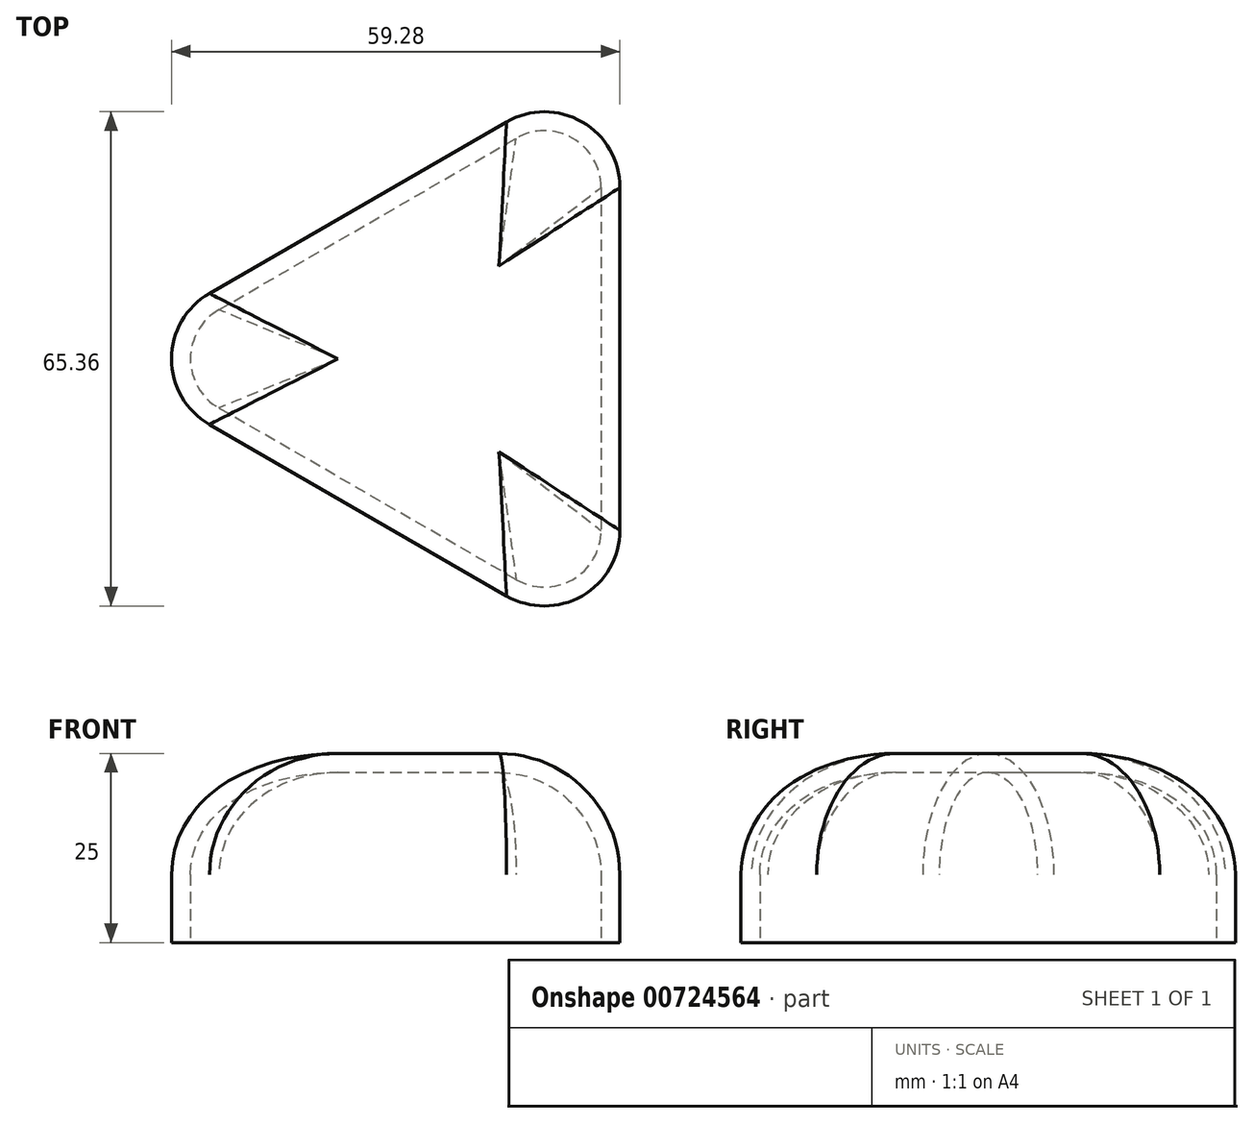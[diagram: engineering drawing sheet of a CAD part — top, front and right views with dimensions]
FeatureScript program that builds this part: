
annotation { "Feature Type Name" : "Feature", "Feature Type Description" : "" }
export const myFeature = defineFeature(function(context is Context, id is Id, definition is map)
    precondition{}
    {
        {
            var Q0;
            Q0=qCreatedBy(makeId("Top.planeOp"),FACE);
            var sketch = newSketch(context, id + "F0", { "sketchPlane" : qUnion([Q0])});
            skCircle(sketch, "E0.cCircle", {"center": v(0, 0) * mm, "radius": 23.1 * mm, "construction": true});
            skLineSegment(sketch, "E0.0", {"start": v(23.1, 40) * mm, "end": v(23.1, -40) * mm});
            skLineSegment(sketch, "E0.1", {"start": v(23.1, -40) * mm, "end": v(-46.19, 0) * mm});
            skLineSegment(sketch, "E0.2", {"start": v(-46.19, 0) * mm, "end": v(23.1, 40) * mm});
            skPoint(sketch, "E0.0.midPoint", {"position": v(23.1, 0) * mm});
            skSolve(sketch);
        }
        {
            var Q0;
            Q0=makeQuery(id+"F0.imprint","IMPRINT",FACE,{"disambiguationData":[TD([[makeQuery(id+"F0.imprint","IMPRINT",EDGE,{"derivedFrom":sQuery(id+"F0.wireOp",EDGE,"E0.0")}),-1.0]])]});
            extrude(context, id + "F1", {"entities" : qUnion([Q0]), "depth" : 25 * mm, "offsetDistance" : 25 * mm});
        }
        {
            var Q0;
            Q0=makeQuery(id+"F1.opExtrude","SWEPT_EDGE",EDGE,{"disambiguationData":[OSD([sQuery(id+"F0.wireOp",EDGE,"E0.0"),sQuery(id+"F0.wireOp",EDGE,"E0.1")])]});
            var Q1;
            Q1=makeQuery(id+"F1.opExtrude","SWEPT_EDGE",EDGE,{"disambiguationData":[OSD([sQuery(id+"F0.wireOp",EDGE,"E0.0"),sQuery(id+"F0.wireOp",EDGE,"E0.2")])]});
            var Q2;
            Q2=makeQuery(id+"F1.opExtrude","SWEPT_EDGE",EDGE,{"disambiguationData":[OSD([sQuery(id+"F0.wireOp",EDGE,"E0.1"),sQuery(id+"F0.wireOp",EDGE,"E0.2")])]});
            fillet(context, id + "F2", {"entities" : qUnion([Q0, Q1, Q2]), "radius" : 10 * mm, "tangentPropagation" : true, "allowEdgeOverflow" : false});
        }
        {
            var Q0;
            {var subQ0=sQuery(id+"F0.wireOp",EDGE,"E0.1");var subQ1=sQuery(id+"F0.wireOp",EDGE,"E0.0");Q0=makeQuery(id+"F2.opFillet","BLEND_EDGE",EDGE,{"blendedFrom":[makeQuery(id+"F1.opExtrude","SWEPT_EDGE",EDGE,{"disambiguationData":[OSD([subQ1,subQ0])]}),makeQuery(id+"F1.opExtrude","CAP_FACE",FACE,{"disambiguationData":[OSD([subQ1,subQ0,sQuery(id+"F0.wireOp",EDGE,"E0.2")])],"isStart":false})],"blendedInto":[makeQuery(id+"F1.opExtrude","CAP_FACE",FACE,{"disambiguationData":[OSD([subQ1,subQ0,sQuery(id+"F0.wireOp",EDGE,"E0.2")])],"isStart":false})]});}
            var Q1;
            Q1=makeQuery(id+"F1.opExtrude","CAP_EDGE",EDGE,{"disambiguationData":[OSD([sQuery(id+"F0.wireOp",EDGE,"E0.0")])],"isStart":false});
            var Q2;
            {var subQ0=sQuery(id+"F0.wireOp",EDGE,"E0.2");var subQ1=sQuery(id+"F0.wireOp",EDGE,"E0.0");Q2=makeQuery(id+"F2.opFillet","BLEND_EDGE",EDGE,{"blendedFrom":[makeQuery(id+"F1.opExtrude","SWEPT_EDGE",EDGE,{"disambiguationData":[OSD([subQ1,subQ0])]}),makeQuery(id+"F1.opExtrude","CAP_FACE",FACE,{"disambiguationData":[OSD([subQ1,sQuery(id+"F0.wireOp",EDGE,"E0.1"),subQ0])],"isStart":false})],"blendedInto":[makeQuery(id+"F1.opExtrude","CAP_FACE",FACE,{"disambiguationData":[OSD([subQ1,sQuery(id+"F0.wireOp",EDGE,"E0.1"),subQ0])],"isStart":false})]});}
            var Q3;
            Q3=makeQuery(id+"F1.opExtrude","CAP_EDGE",EDGE,{"disambiguationData":[OSD([sQuery(id+"F0.wireOp",EDGE,"E0.2")])],"isStart":false});
            var Q4;
            {var subQ0=sQuery(id+"F0.wireOp",EDGE,"E0.2");var subQ1=sQuery(id+"F0.wireOp",EDGE,"E0.1");Q4=makeQuery(id+"F2.opFillet","BLEND_EDGE",EDGE,{"blendedFrom":[makeQuery(id+"F1.opExtrude","SWEPT_EDGE",EDGE,{"disambiguationData":[OSD([subQ1,subQ0])]}),makeQuery(id+"F1.opExtrude","CAP_FACE",FACE,{"disambiguationData":[OSD([sQuery(id+"F0.wireOp",EDGE,"E0.0"),subQ1,subQ0])],"isStart":false})],"blendedInto":[makeQuery(id+"F1.opExtrude","CAP_FACE",FACE,{"disambiguationData":[OSD([sQuery(id+"F0.wireOp",EDGE,"E0.0"),subQ1,subQ0])],"isStart":false})]});}
            var Q5;
            Q5=makeQuery(id+"F1.opExtrude","CAP_EDGE",EDGE,{"disambiguationData":[OSD([sQuery(id+"F0.wireOp",EDGE,"E0.1")])],"isStart":false});
            fillet(context, id + "F3", {"entities" : qUnion([Q0, Q1, Q2, Q3, Q4, Q5]), "radius" : 16 * mm, "tangentPropagation" : true, "allowEdgeOverflow" : false});
        }
        {
            var Q0;
            Q0=makeQuery(id+"F1.opExtrude","CAP_FACE",FACE,{"disambiguationData":[OSD([sQuery(id+"F0.wireOp",EDGE,"E0.0"),sQuery(id+"F0.wireOp",EDGE,"E0.1"),sQuery(id+"F0.wireOp",EDGE,"E0.2")])],"isStart":true});
            shell(context, id + "F4", {"entities" : qUnion([Q0]), "thickness" : 2.5 * mm});
        }
    });
